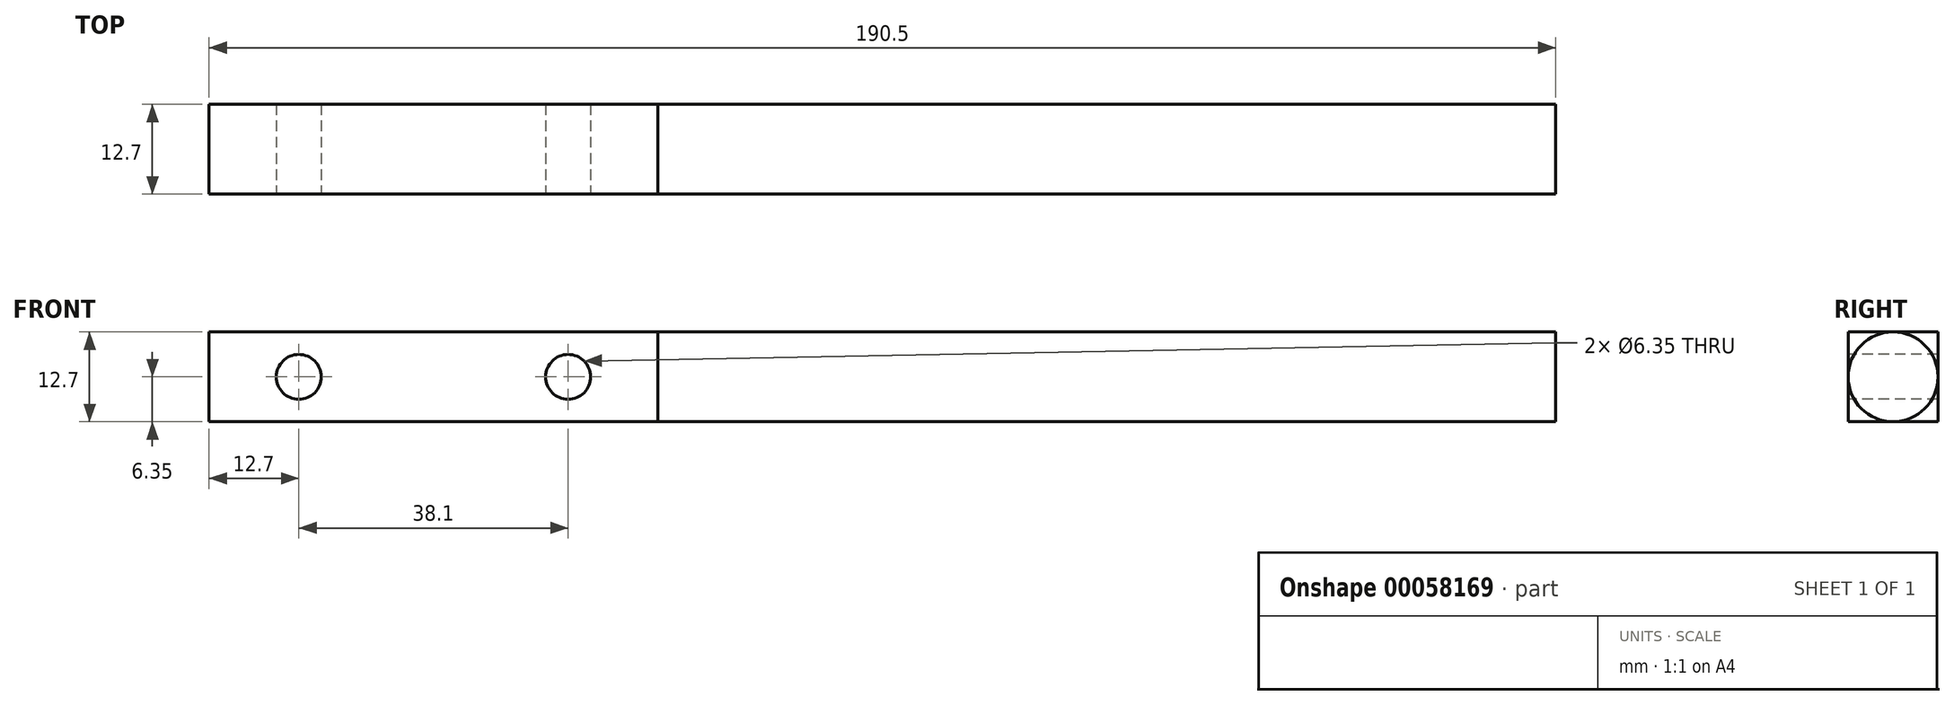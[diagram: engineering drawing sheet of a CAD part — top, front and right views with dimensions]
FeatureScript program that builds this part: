
annotation { "Feature Type Name" : "Feature", "Feature Type Description" : "" }
export const myFeature = defineFeature(function(context is Context, id is Id, definition is map)
    precondition{}
    {
        {
            var Q0;
            Q0=qCreatedBy(makeId("Right.planeOp"),FACE);
            var sketch = newSketch(context, id + "F0", { "sketchPlane" : qUnion([Q0])});
            skLineSegment(sketch, "E0.rect.bottom", {"start": v(6.35, 6.35) * mm, "end": v(-6.35, 6.35) * mm});
            skLineSegment(sketch, "E0.rect.top", {"start": v(6.35, -6.35) * mm, "end": v(-6.35, -6.35) * mm});
            skLineSegment(sketch, "E0.rect.left", {"start": v(6.35, 6.35) * mm, "end": v(6.35, -6.35) * mm});
            skLineSegment(sketch, "E0.rect.right", {"start": v(-6.35, 6.35) * mm, "end": v(-6.35, -6.35) * mm});
            skPoint(sketch, "E0.rect.middle", {"position": v(0, 0) * mm});
            skSolve(sketch);
        }
        {
            var Q0;
            Q0=qCreatedBy(makeId("Right.planeOp"),FACE);
            var sketch = newSketch(context, id + "F1", { "sketchPlane" : qUnion([Q0])});
            skCircle(sketch, "E1", {"center": v(0, 0) * mm, "radius": 6.35 * mm});
            skSolve(sketch);
        }
        {
            var Q0;
            Q0 = qSketchRegion(id + "F0", true);
            extrude(context, id + "F2", {"entities" : qUnion([Q0]), "oppositeDirection" : true, "depth" : 63.5 * mm});
        }
        {
            var Q0;
            Q0 = qSketchRegion(id + "F1", true);
            extrude(context, id + "F3", {"entities" : qUnion([Q0]), "operationType" : NewBodyOperationType.ADD, "depth" : 127 * mm});
        }
        {
            var Q0;
            Q0=makeQuery(id+"F2.opExtrude","SWEPT_FACE",FACE,{"disambiguationData":[OSD([sQuery(id+"F0.wireOp",EDGE,"E0.rect.right")])]});
            var sketch = newSketch(context, id + "F4", { "sketchPlane" : qUnion([Q0])});
            skCircle(sketch, "E2", {"center": v(-50.8, 0) * mm, "radius": 3.18 * mm});
            skCircle(sketch, "E3", {"center": v(-12.7, 0) * mm, "radius": 3.18 * mm});
            skSolve(sketch);
        }
        {
            var Q0;
            Q0 = qSketchRegion(id + "F4", true);
            extrude(context, id + "F5", {"entities" : qUnion([Q0]), "operationType" : NewBodyOperationType.REMOVE, "oppositeDirection" : true, "depth" : 25.4 * mm});
        }
    });
